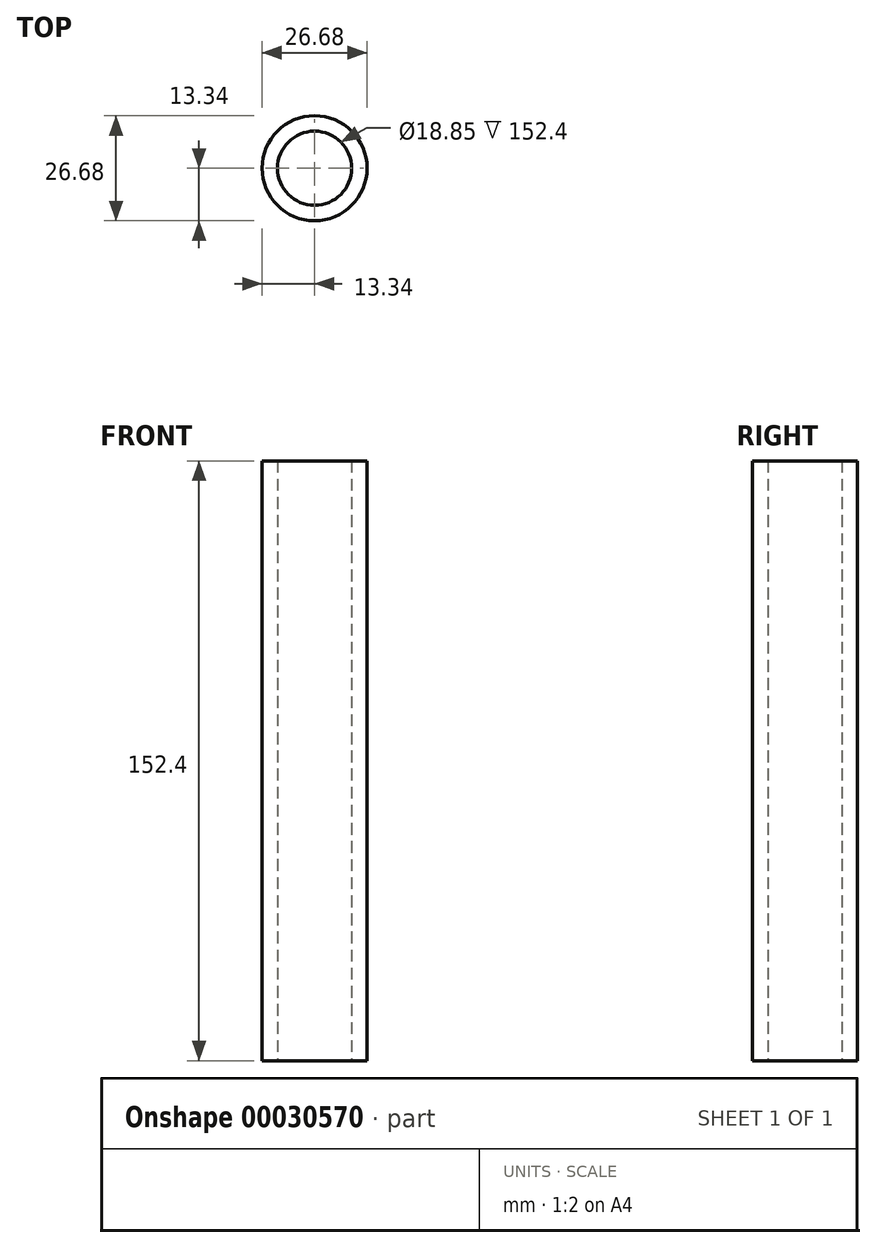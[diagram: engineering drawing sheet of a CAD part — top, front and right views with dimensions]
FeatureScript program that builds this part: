
annotation { "Feature Type Name" : "Feature", "Feature Type Description" : "" }
export const myFeature = defineFeature(function(context is Context, id is Id, definition is map)
    precondition{}
    {
        {
            var Q0;
            Q0=qCreatedBy(makeId("Top.planeOp"),FACE);
            var sketch = newSketch(context, id + "F0", { "sketchPlane" : qUnion([Q0])});
            skCircle(sketch, "E0", {"center": v(0, 0) * mm, "radius": 13.34 * mm});
            skCircle(sketch, "E1.0", {"center": v(0, 0) * mm, "radius": 9.42 * mm});
            skSolve(sketch);
        }
        {
            var Q0;
            Q0 = qSketchRegion(id + "F0", true);
            extrude(context, id + "F1", {"entities" : qUnion([Q0]), "endBound" : BoundingType.SYMMETRIC, "depth" : 152.4 * mm});
        }
    });
